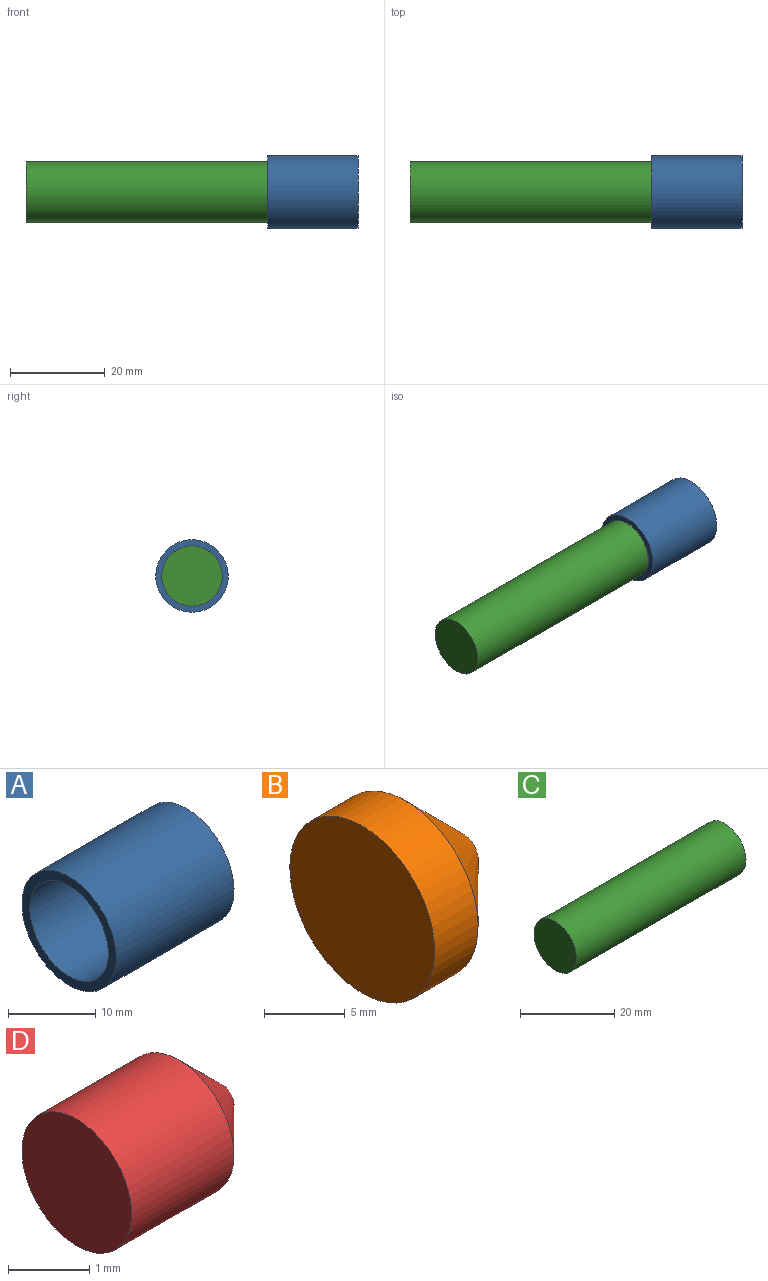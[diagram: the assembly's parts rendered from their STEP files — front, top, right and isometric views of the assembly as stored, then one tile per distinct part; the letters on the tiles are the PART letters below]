
ASSEMBLY  parts=4 mates=3
PART A: 5 faces, bbox 19.1x15.2x15.2 mm
  f0: cylinder r=7.62mm len=19.05mm, axis (-1,0,0), area 912.1mm2, adj f1,f2
  f1: plane 15.24x15.24mm, normal (1,0,0), area 182.4mm2, adj f0
  f2: plane 15.24x15.24mm, normal (-1,0,0), area 55.7mm2, adj f0,f3
  f3: cylinder r=6.35mm len=17.78mm, axis (-1,0,0), area 709.4mm2, adj f2,f4
  f4: plane 12.7x12.7mm, normal (-1,0,0), area 126.7mm2, adj f3
PART B: 4 faces, bbox 8.9x12.7x12.7 mm
  f0: cylinder r=6.35mm len=12.7mm, axis (-1,0,0), area 152mm2, adj f2,f3
  f1: plane 2.54x2.54mm, normal (1,0,0), area 5.1mm2, adj f3
  f2: plane 12.7x12.7mm, normal (-1,0,0), area 126.7mm2, adj f0
  f3: cone r=1.27mm half-angle=45deg, axis (-1,0,0), area 172mm2, adj f0,f1
PART C: 3 faces, bbox 50.8x12.7x12.7 mm
  f0: cylinder r=6.35mm len=50.8mm, axis (-1,0,0), area 2026.8mm2, adj f1,f2
  f1: plane 12.7x12.7mm, normal (1,0,0), area 126.7mm2, adj f0
  f2: plane 12.7x12.7mm, normal (-1,0,0), area 126.7mm2, adj f0
PART D: 4 faces, bbox 2.5x1.9x1.9 mm
  f0: cylinder r=0.95mm len=1.91mm, axis (-1,0,0), area 10.6mm2, adj f2,f3
  f1: plane 0.38x0.38mm, normal (1,0,0), area 0.1mm2, adj f3
  f2: plane 1.91x1.91mm, normal (-1,0,0), area 2.9mm2, adj f0
  f3: cone r=0.19mm half-angle=45deg, axis (-1,0,0), area 3.9mm2, adj f0,f1
PLACE A rot(axis=(1,0,0),0deg) t=(-94.02,-45.42,-14.86)mm
PLACE B rot(axis=(1,0,0),0deg) t=(-94.1,31.71,-15.45)mm
PLACE C rot(axis=(1,0,0),0deg) t=(-144.9,-12.59,-7.74)mm
PLACE D rot(axis=(1,0,0),0deg) t=(-85.21,14.24,4.39)mm
MATE fastened B.f0 <-> C.f0  axis (-1,0,0) through (-94.1,-27.22,17)mm
MATE fastened D.f0 <-> B.f0  axis (-1,0,0) through (-85.21,-27.22,17)mm
MATE slider A.f0 <-> D.f0  axis (-1,0,0) through (-85.13,-27.22,17)mm
